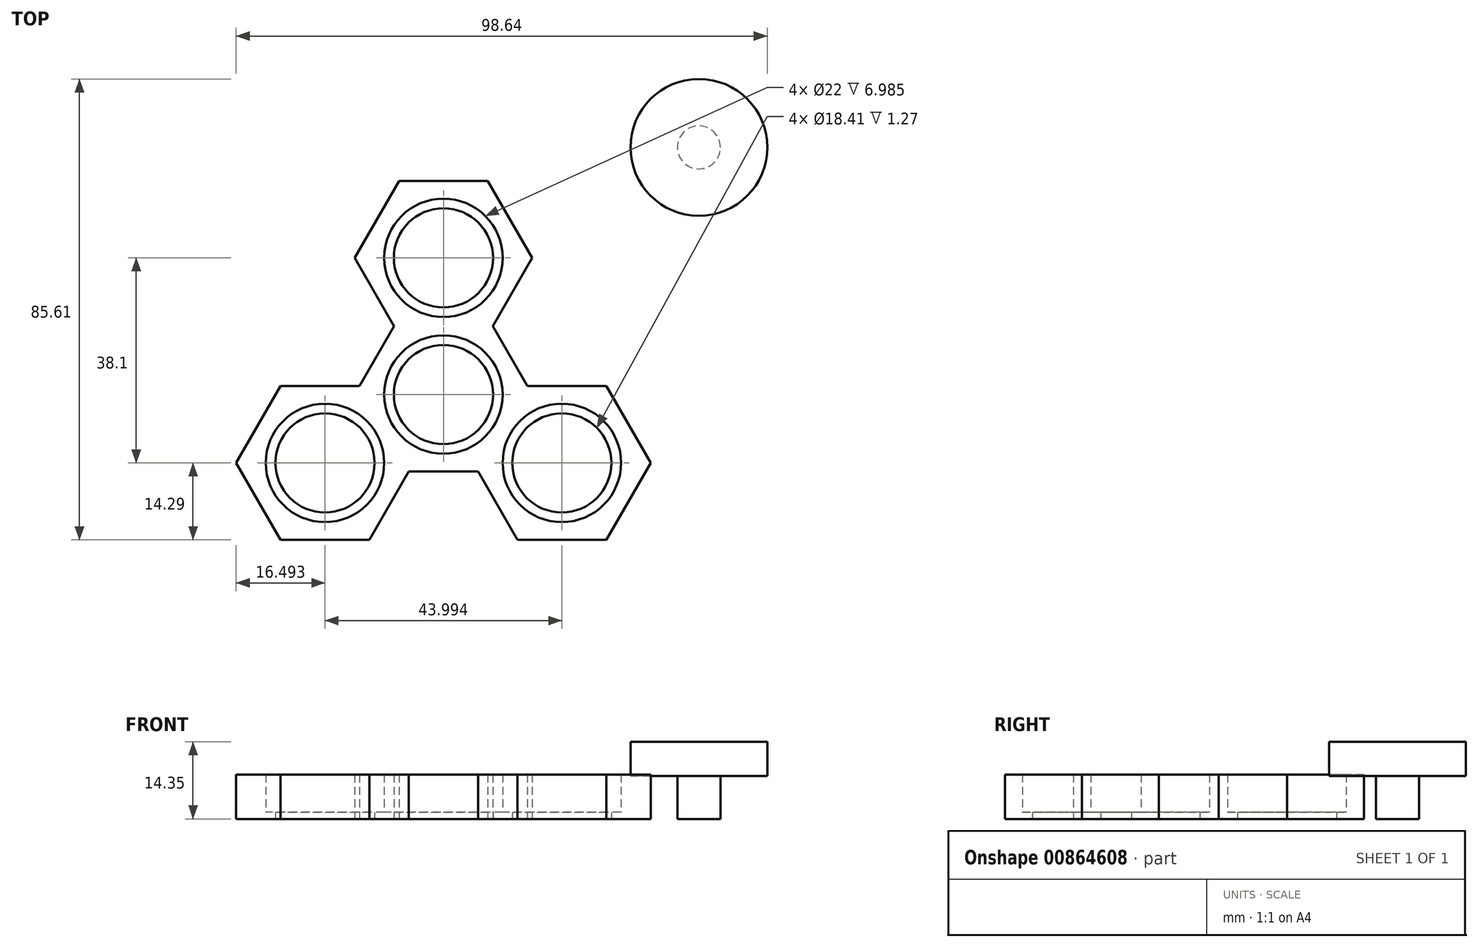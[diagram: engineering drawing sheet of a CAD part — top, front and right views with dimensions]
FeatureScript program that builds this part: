
annotation { "Feature Type Name" : "Feature", "Feature Type Description" : "" }
export const myFeature = defineFeature(function(context is Context, id is Id, definition is map)
    precondition{}
    {
        {
            var Q0;
            Q0=qCreatedBy(makeId("Top.planeOp"),FACE);
            var sketch = newSketch(context, id + "F0", { "sketchPlane" : qUnion([Q0])});
            skLineSegment(sketch, "E0", {"start": v(0, 0) * mm, "end": v(22, -12.7) * mm, "construction": true});
            skLineSegment(sketch, "E1", {"start": v(0, 0) * mm, "end": v(-22, -12.7) * mm, "construction": true});
            skLineSegment(sketch, "E2", {"start": v(0, 0) * mm, "end": v(0, 25.4) * mm, "construction": true});
            skCircle(sketch, "E3", {"center": v(0, 25.4) * mm, "radius": 11 * mm});
            skCircle(sketch, "E4", {"center": v(22, -12.7) * mm, "radius": 11 * mm});
            skCircle(sketch, "E5", {"center": v(0, 0) * mm, "radius": 11 * mm});
            skCircle(sketch, "E6", {"center": v(-22, -12.7) * mm, "radius": 11 * mm});
            skCircle(sketch, "E7.cCircle", {"center": v(0, 25.4) * mm, "radius": 14.29 * mm, "construction": true});
            skLineSegment(sketch, "E7.0", {"start": v(-8.25, 39.69) * mm, "end": v(8.25, 39.69) * mm});
            skLineSegment(sketch, "E7.1", {"start": v(8.25, 39.69) * mm, "end": v(16.5, 25.4) * mm});
            skLineSegment(sketch, "E7.2", {"start": v(16.5, 25.4) * mm, "end": v(9.17, 12.7) * mm});
            skLineSegment(sketch, "E7.5", {"start": v(-16.5, 25.4) * mm, "end": v(-8.25, 39.69) * mm});
            skPoint(sketch, "E7.0.midPoint", {"position": v(0, 39.69) * mm});
            skCircle(sketch, "E8.cCircle", {"center": v(22, -12.7) * mm, "radius": 14.29 * mm, "construction": true});
            skLineSegment(sketch, "E8.0", {"start": v(30.25, -26.99) * mm, "end": v(13.75, -26.99) * mm});
            skLineSegment(sketch, "E8.1", {"start": v(13.75, -26.99) * mm, "end": v(6.42, -14.29) * mm});
            skLineSegment(sketch, "E8.3", {"start": v(13.75, 1.59) * mm, "end": v(14.2, 1.59) * mm});
            skLineSegment(sketch, "E8.4", {"start": v(30.25, 1.59) * mm, "end": v(38.5, -12.7) * mm});
            skLineSegment(sketch, "E8.5", {"start": v(38.5, -12.7) * mm, "end": v(30.25, -26.99) * mm});
            skPoint(sketch, "E8.0.midPoint", {"position": v(22, -26.99) * mm});
            skCircle(sketch, "E9.cCircle", {"center": v(-22, -12.7) * mm, "radius": 14.29 * mm, "construction": true});
            skLineSegment(sketch, "E9.0", {"start": v(-30.25, -26.99) * mm, "end": v(-38.5, -12.7) * mm});
            skLineSegment(sketch, "E9.1", {"start": v(-38.5, -12.7) * mm, "end": v(-30.25, 1.59) * mm});
            skLineSegment(sketch, "E9.2", {"start": v(-30.25, 1.59) * mm, "end": v(-15.58, 1.59) * mm});
            skLineSegment(sketch, "E9.5", {"start": v(-13.75, -26.99) * mm, "end": v(-30.25, -26.99) * mm});
            skPoint(sketch, "E9.0.midPoint", {"position": v(-34.37, -19.84) * mm});
            skCircle(sketch, "E10.cCircle", {"center": v(0, 0) * mm, "radius": 14.29 * mm, "construction": true});
            skPoint(sketch, "E10.0.midPoint", {"position": v(0, -14.29) * mm});
            skPoint(sketch, "E11.orphan", {"position": v(-8.25, 14.29) * mm});
            skLineSegment(sketch, "E12.trimOffspring", {"start": v(9.17, 12.7) * mm, "end": v(15.58, 1.59) * mm});
            skLineSegment(sketch, "E13.trimOffspring", {"start": v(-9.17, 12.7) * mm, "end": v(-16.5, 25.4) * mm});
            skLineSegment(sketch, "E14.trimOffspring", {"start": v(-15.58, 1.59) * mm, "end": v(-9.17, 12.7) * mm});
            skPoint(sketch, "E15.orphan", {"position": v(-13.75, 1.59) * mm});
            skPoint(sketch, "E16.trimOffspring.end.orphan", {"position": v(-8.25, -14.29) * mm});
            skLineSegment(sketch, "E17.trimOffspring", {"start": v(-6.42, -14.29) * mm, "end": v(-13.75, -26.99) * mm});
            skLineSegment(sketch, "E18.trimOffspring", {"start": v(6.42, -14.29) * mm, "end": v(-6.42, -14.29) * mm});
            skPoint(sketch, "E19.orphan", {"position": v(5.5, -12.7) * mm});
            skLineSegment(sketch, "E20.trimOffspring", {"start": v(15.58, 1.59) * mm, "end": v(30.25, 1.59) * mm});
            skPoint(sketch, "E10.0.start.orphan", {"position": v(8.25, -14.29) * mm});
            skSolve(sketch);
        }
        {
            var Q0;
            Q0 = qSketchRegion(id + "F0", true);
            extrude(context, id + "F1", {"entities" : qUnion([Q0]), "depth" : 8.25 * mm, "offsetDistance" : 25.4 * mm});
        }
        {
            var Q0;
            Q0=qCreatedBy(makeId("Top.planeOp"),FACE);
            var sketch = newSketch(context, id + "F2", { "sketchPlane" : qUnion([Q0])});
            skCircle(sketch, "E21", {"center": v(47.45, 45.92) * mm, "radius": 4 * mm});
            skSolve(sketch);
        }
        {
            var Q0;
            Q0 = qSketchRegion(id + "F2", true);
            extrude(context, id + "F3", {"entities" : qUnion([Q0]), "depth" : 8 * mm, "offsetDistance" : 25.4 * mm});
        }
        {
            var Q0;
            Q0=makeQuery(id+"F3.opExtrude","CAP_FACE",FACE,{"disambiguationData":[OSD([sQuery(id+"F2.wireOp",EDGE,"E21")])],"isStart":false});
            var sketch = newSketch(context, id + "F4", { "sketchPlane" : qUnion([Q0])});
            skCircle(sketch, "E22", {"center": v(47.45, 45.92) * mm, "radius": 12.7 * mm});
            skSolve(sketch);
        }
        {
            var Q0;
            Q0 = qSketchRegion(id + "F4", true);
            extrude(context, id + "F5", {"entities" : qUnion([Q0]), "operationType" : NewBodyOperationType.ADD, "depth" : 6.35 * mm, "offsetDistance" : 25.4 * mm});
        }
        {
            var Q0;
            Q0=makeQuery(id+"F1.opExtrude","CAP_FACE",FACE,{"disambiguationData":[OSD([sQuery(id+"F0.wireOp",EDGE,"E3"),sQuery(id+"F0.wireOp",EDGE,"E4"),sQuery(id+"F0.wireOp",EDGE,"E5"),sQuery(id+"F0.wireOp",EDGE,"E6"),sQuery(id+"F0.wireOp",EDGE,"E7.0"),sQuery(id+"F0.wireOp",EDGE,"E7.1"),sQuery(id+"F0.wireOp",EDGE,"E7.2"),sQuery(id+"F0.wireOp",EDGE,"E7.5"),sQuery(id+"F0.wireOp",EDGE,"E8.0"),sQuery(id+"F0.wireOp",EDGE,"E8.1"),sQuery(id+"F0.wireOp",EDGE,"E8.4"),sQuery(id+"F0.wireOp",EDGE,"E8.5"),sQuery(id+"F0.wireOp",EDGE,"E9.0"),sQuery(id+"F0.wireOp",EDGE,"E9.1"),sQuery(id+"F0.wireOp",EDGE,"E9.2"),sQuery(id+"F0.wireOp",EDGE,"E9.5"),sQuery(id+"F0.wireOp",EDGE,"E12.trimOffspring"),sQuery(id+"F0.wireOp",EDGE,"E13.trimOffspring"),sQuery(id+"F0.wireOp",EDGE,"E14.trimOffspring"),sQuery(id+"F0.wireOp",EDGE,"E17.trimOffspring"),sQuery(id+"F0.wireOp",EDGE,"E18.trimOffspring"),sQuery(id+"F0.wireOp",EDGE,"E20.trimOffspring")])],"isStart":true});
            var sketch = newSketch(context, id + "F6", { "sketchPlane" : qUnion([Q0])});
            skCircle(sketch, "E23.0", {"center": v(-22, 12.7) * mm, "radius": 11 * mm});
            skCircle(sketch, "E24.0", {"center": v(22, 12.7) * mm, "radius": 11 * mm});
            skCircle(sketch, "E25.0", {"center": v(0, 0) * mm, "radius": 11 * mm});
            skCircle(sketch, "E26.0", {"center": v(0, -25.4) * mm, "radius": 11 * mm});
            skCircle(sketch, "E27", {"center": v(-22, 12.7) * mm, "radius": 9.2 * mm});
            skCircle(sketch, "E28", {"center": v(0, 0) * mm, "radius": 9.2 * mm});
            skCircle(sketch, "E29", {"center": v(22, 12.7) * mm, "radius": 9.2 * mm});
            skCircle(sketch, "E30", {"center": v(0, -25.4) * mm, "radius": 9.2 * mm});
            skSolve(sketch);
        }
        {
            var Q0;
            Q0 = qSketchRegion(id + "F6", true);
            extrude(context, id + "F7", {"entities" : qUnion([Q0]), "operationType" : NewBodyOperationType.ADD, "oppositeDirection" : true, "depth" : 1.27 * mm, "offsetDistance" : 25.4 * mm});
        }
    });
